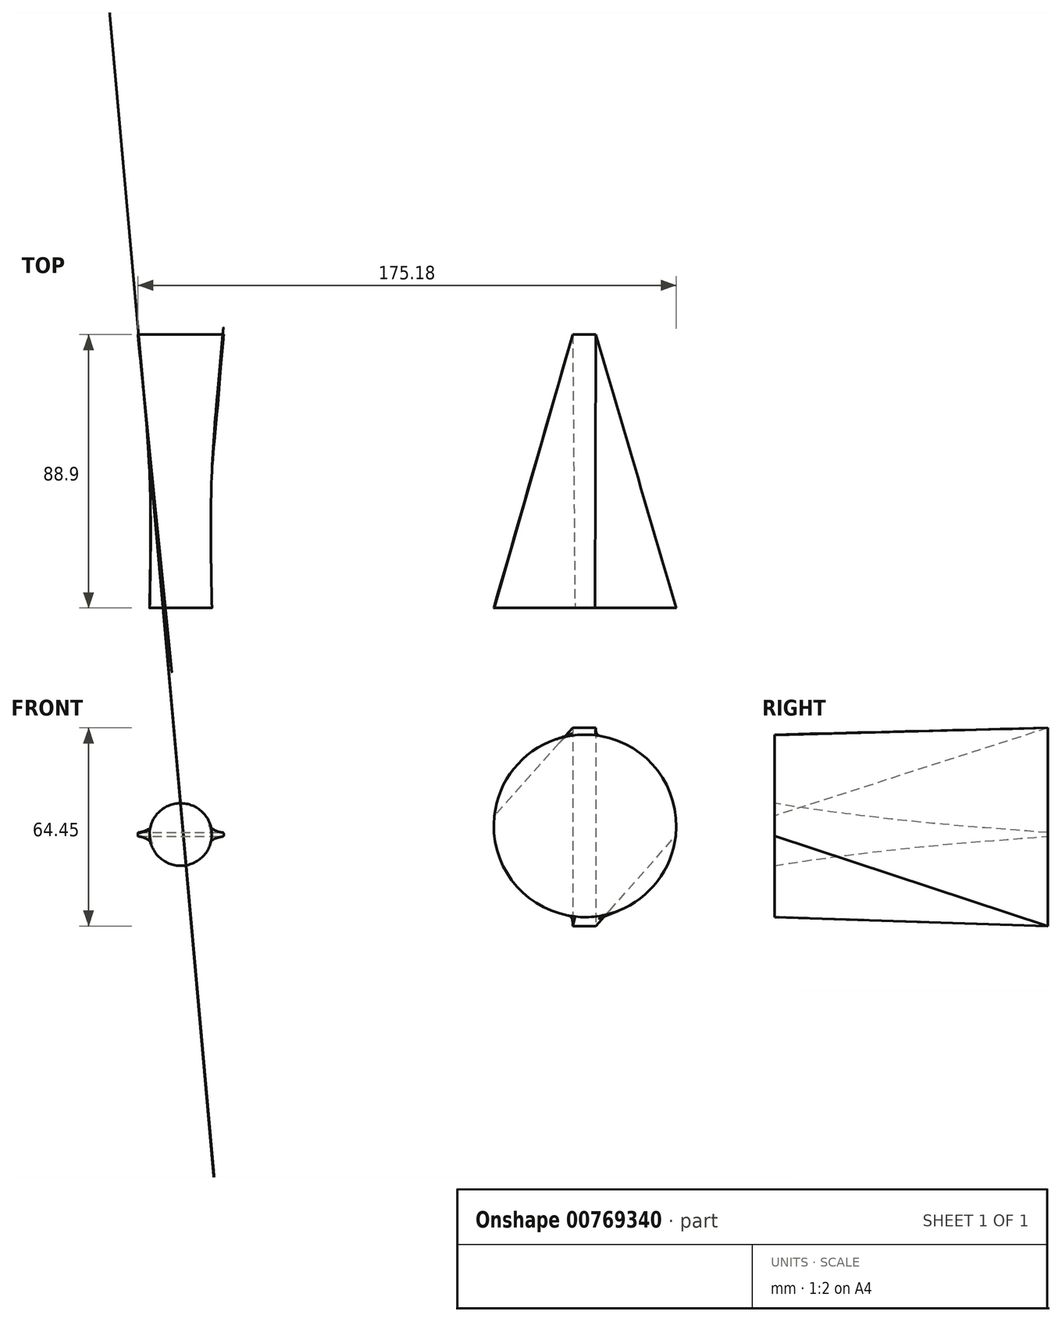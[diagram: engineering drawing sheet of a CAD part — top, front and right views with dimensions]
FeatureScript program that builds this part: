
annotation { "Feature Type Name" : "Feature", "Feature Type Description" : "" }
export const myFeature = defineFeature(function(context is Context, id is Id, definition is map)
    precondition{}
    {
        {
            var Q0;
            Q0=qCreatedBy(makeId("Front.planeOp"),FACE);
            cPlane(context, id + "F0", {"entities" : qUnion([Q0]), "cplaneType" : CPlaneType.OFFSET, "offset" : 88.9 * mm, "width" : 152.4 * mm, "height" : 152.4 * mm});
        }
        {
            var Q0;
            Q0=qCreatedBy(makeId("Front.planeOp"),FACE);
            var sketch = newSketch(context, id + "F1", { "sketchPlane" : qUnion([Q0])});
            skLineSegment(sketch, "E0.bottom", {"start": v(0.25, 0) * mm, "end": v(27.69, 0) * mm});
            skLineSegment(sketch, "E0.top", {"start": v(0.25, 1.27) * mm, "end": v(27.69, 1.27) * mm});
            skLineSegment(sketch, "E0.left", {"start": v(0, 0.25) * mm, "end": v(0, 1.02) * mm});
            skLineSegment(sketch, "E0.right", {"start": v(27.94, 0.25) * mm, "end": v(27.94, 1.02) * mm});
            skPoint(sketch, "E1.visualSharp", {"position": v(0, 1.27) * mm});
            skArc(sketch, "E1.filletArc", {"start": v(0.25, 1.27) * mm, "mid": v(0.07, 1.2) * mm, "end": v(0, 1.02) * mm});
            skPoint(sketch, "E2.visualSharp", {"position": v(0, 0) * mm});
            skArc(sketch, "E2.filletArc", {"start": v(0, 0.25) * mm, "mid": v(0.07, 0.07) * mm, "end": v(0.25, 0) * mm});
            skPoint(sketch, "E3.visualSharp", {"position": v(27.94, 0) * mm});
            skArc(sketch, "E3.filletArc", {"start": v(27.69, 0) * mm, "mid": v(27.87, 0.07) * mm, "end": v(27.94, 0.25) * mm});
            skPoint(sketch, "E4.visualSharp", {"position": v(27.94, 1.27) * mm});
            skArc(sketch, "E4.filletArc", {"start": v(27.94, 1.02) * mm, "mid": v(27.87, 1.2) * mm, "end": v(27.69, 1.27) * mm});
            skSolve(sketch);
        }
        {
            var Q0;
            Q0=qCreatedBy(id+"F0.planeOp",FACE);
            var sketch = newSketch(context, id + "F2", { "sketchPlane" : qUnion([Q0])});
            skCircle(sketch, "E5", {"center": v(13.97, 0.64) * mm, "radius": 10.16 * mm});
            skSolve(sketch);
        }
        {
            var Q0;
            Q0=qCreatedBy(makeId("Front.planeOp"),FACE);
            cPlane(context, id + "F3", {"entities" : qUnion([Q0]), "cplaneType" : CPlaneType.OFFSET, "offset" : 44.45 * mm, "width" : 152.4 * mm, "height" : 152.4 * mm});
        }
        {
            var Q0;
            Q0=qCreatedBy(id+"F3.planeOp",FACE);
            var sketch = newSketch(context, id + "F4", { "sketchPlane" : qUnion([Q0])});
            skLineSegment(sketch, "E6", {"start": v(3.81, 2) * mm, "end": v(3.81, -0.72) * mm});
            skLineSegment(sketch, "E7", {"start": v(24.13, 2) * mm, "end": v(24.13, -0.72) * mm});
            skArc(sketch, "E8", {"start": v(23.33, 3.18) * mm, "mid": v(13.97, 4.96) * mm, "end": v(4.61, 3.18) * mm});
            skArc(sketch, "E9", {"start": v(4.61, -1.9) * mm, "mid": v(13.97, -3.7) * mm, "end": v(23.33, -1.9) * mm});
            skLineSegment(sketch, "E10", {"start": v(13.97, 12.88) * mm, "end": v(13.97, -15.57) * mm, "construction": true});
            skLineSegment(sketch, "E11", {"start": v(8.81, 0.64) * mm, "end": v(21.36, 0.64) * mm, "construction": true});
            skPoint(sketch, "E12.visualSharp", {"position": v(24.13, 2.84) * mm});
            skArc(sketch, "E12.filletArc", {"start": v(24.13, 2) * mm, "mid": v(23.91, 2.7) * mm, "end": v(23.33, 3.18) * mm});
            skPoint(sketch, "E13.visualSharp", {"position": v(24.13, -1.57) * mm});
            skArc(sketch, "E13.filletArc", {"start": v(23.33, -1.9) * mm, "mid": v(23.91, -1.44) * mm, "end": v(24.13, -0.72) * mm});
            skPoint(sketch, "E14.visualSharp", {"position": v(3.81, -1.57) * mm});
            skArc(sketch, "E14.filletArc", {"start": v(3.81, -0.72) * mm, "mid": v(4.03, -1.44) * mm, "end": v(4.61, -1.9) * mm});
            skPoint(sketch, "E15.visualSharp", {"position": v(3.81, 2.84) * mm});
            skArc(sketch, "E15.filletArc", {"start": v(4.61, 3.18) * mm, "mid": v(4.03, 2.7) * mm, "end": v(3.81, 2) * mm});
            skSolve(sketch);
        }
        {
            var Q0;
            Q0=makeQuery(id+"F2.imprint","IMPRINT",FACE,{"disambiguationData":[TD([[makeQuery(id+"F2.imprint","IMPRINT",EDGE,{"derivedFrom":sQuery(id+"F2.wireOp",EDGE,"E5")}),1.0]])]});
            var Q1;
            Q1=makeQuery(id+"F4.imprint","IMPRINT",FACE,{"disambiguationData":[TD([[makeQuery(id+"F4.imprint","IMPRINT",EDGE,{"derivedFrom":sQuery(id+"F4.wireOp",EDGE,"E6")}),1.0]])]});
            var Q2;
            Q2 = qSketchRegion(id + "F1", true);
            loft(context, id + "F5", {"sheetProfilesArray" : [{ "sheetProfileEntities" : qUnion([Q0]) }, { "sheetProfileEntities" : qUnion([Q1]) }, { "sheetProfileEntities" : qUnion([Q2]) }]});
        }
        {
            var Q0;
            Q0=qCreatedBy(makeId("Front.planeOp"),FACE);
            var sketch = newSketch(context, id + "F6", { "sketchPlane" : qUnion([Q0])});
            skLineSegment(sketch, "E16.bottom", {"start": v(149.03, 35.3) * mm, "end": v(141.5, 35.3) * mm});
            skLineSegment(sketch, "E16.top", {"start": v(149.03, -29.15) * mm, "end": v(141.5, -29.15) * mm});
            skLineSegment(sketch, "E16.left", {"start": v(149.03, 35.3) * mm, "end": v(149.03, -29.15) * mm});
            skLineSegment(sketch, "E16.right", {"start": v(141.5, 35.3) * mm, "end": v(141.5, -29.15) * mm});
            skSolve(sketch);
        }
        {
            var Q0;
            Q0=qCreatedBy(id+"F0.planeOp",FACE);
            var sketch = newSketch(context, id + "F7", { "sketchPlane" : qUnion([Q0])});
            skCircle(sketch, "E17", {"center": v(145.5, 3.44) * mm, "radius": 29.67 * mm});
            skSolve(sketch);
        }
        {
            var Q0;
            Q0=makeQuery(id+"F6.imprint","IMPRINT",FACE,{"disambiguationData":[TD([[makeQuery(id+"F6.imprint","IMPRINT",EDGE,{"derivedFrom":sQuery(id+"F6.wireOp",EDGE,"E16.bottom")}),1.0]])]});
            var Q1;
            Q1=makeQuery(id+"F7.imprint","IMPRINT",FACE,{"disambiguationData":[TD([[makeQuery(id+"F7.imprint","IMPRINT",EDGE,{"derivedFrom":sQuery(id+"F7.wireOp",EDGE,"E17")}),1.0]])]});
            loft(context, id + "F8", {"sheetProfilesArray" : [{ "sheetProfileEntities" : qUnion([Q0]) }, { "sheetProfileEntities" : qUnion([Q1]) }]});
        }
    });
